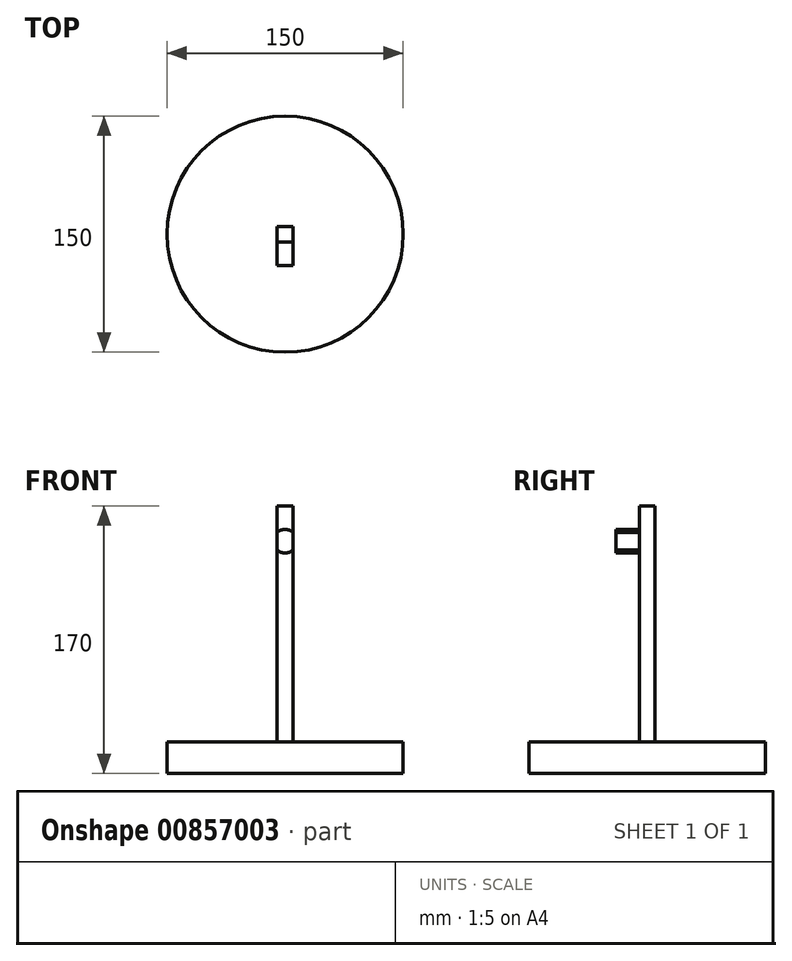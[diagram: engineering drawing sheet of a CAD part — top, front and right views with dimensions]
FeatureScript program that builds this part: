
annotation { "Feature Type Name" : "Feature", "Feature Type Description" : "" }
export const myFeature = defineFeature(function(context is Context, id is Id, definition is map)
    precondition{}
    {
        {
            var Q0;
            Q0=qCreatedBy(makeId("Top.planeOp"),FACE);
            var sketch = newSketch(context, id + "F0", { "sketchPlane" : qUnion([Q0])});
            skCircle(sketch, "E0", {"center": v(0, 0) * mm, "radius": 75 * mm});
            skSolve(sketch);
        }
        {
            var Q0;
            Q0=makeQuery(id+"F0.imprint","IMPRINT",FACE,{"disambiguationData":[TD([[makeQuery(id+"F0.imprint","IMPRINT",EDGE,{"derivedFrom":sQuery(id+"F0.wireOp",EDGE,"E0")}),1.0]])]});
            extrude(context, id + "F1", {"entities" : qUnion([Q0]), "depth" : 20 * mm, "offsetDistance" : 25 * mm});
        }
        {
            var Q0;
            Q0=makeQuery(id+"F1.opExtrude","CAP_FACE",FACE,{"disambiguationData":[OSD([sQuery(id+"F0.wireOp",EDGE,"E0")])],"isStart":false});
            var sketch = newSketch(context, id + "F2", { "sketchPlane" : qUnion([Q0])});
            skLineSegment(sketch, "E1.bottom", {"start": v(5, -5) * mm, "end": v(-5, -5) * mm});
            skLineSegment(sketch, "E1.top", {"start": v(5, 5) * mm, "end": v(-5, 5) * mm});
            skLineSegment(sketch, "E1.left", {"start": v(5, -5) * mm, "end": v(5, 5) * mm});
            skLineSegment(sketch, "E1.right", {"start": v(-5, -5) * mm, "end": v(-5, 5) * mm});
            skPoint(sketch, "E1.middle", {"position": v(0, 0) * mm});
            skSolve(sketch);
        }
        {
            var Q0;
            Q0=makeQuery(id+"F2.imprint","IMPRINT",FACE,{"disambiguationData":[TD([[makeQuery(id+"F2.imprint","IMPRINT",EDGE,{"derivedFrom":sQuery(id+"F2.wireOp",EDGE,"E1.bottom")}),-1.0]])]});
            extrude(context, id + "F3", {"entities" : qUnion([Q0]), "depth" : 150 * mm, "offsetDistance" : 25 * mm});
        }
        {
            var Q0;
            Q0=makeQuery(id+"F3.opExtrude","SWEPT_FACE",FACE,{"disambiguationData":[OSD([sQuery(id+"F2.wireOp",EDGE,"E1.bottom")])]});
            var sketch = newSketch(context, id + "F4", { "sketchPlane" : qUnion([Q0])});
            skCircle(sketch, "E2", {"center": v(0, 147.5) * mm, "radius": 7.5 * mm});
            skSolve(sketch);
        }
        {
            var Q0;
            Q0=makeQuery(id+"F4.imprint","IMPRINT",FACE,{"disambiguationData":[TD([[makeQuery(id+"F4.imprint","IMPRINT",EDGE,{"derivedFrom":sQuery(id+"F4.wireOp",EDGE,"E2")}),1.0]])]});
            extrude(context, id + "F5", {"entities" : qUnion([Q0]), "depth" : 15 * mm, "offsetDistance" : 25 * mm});
        }
    });
